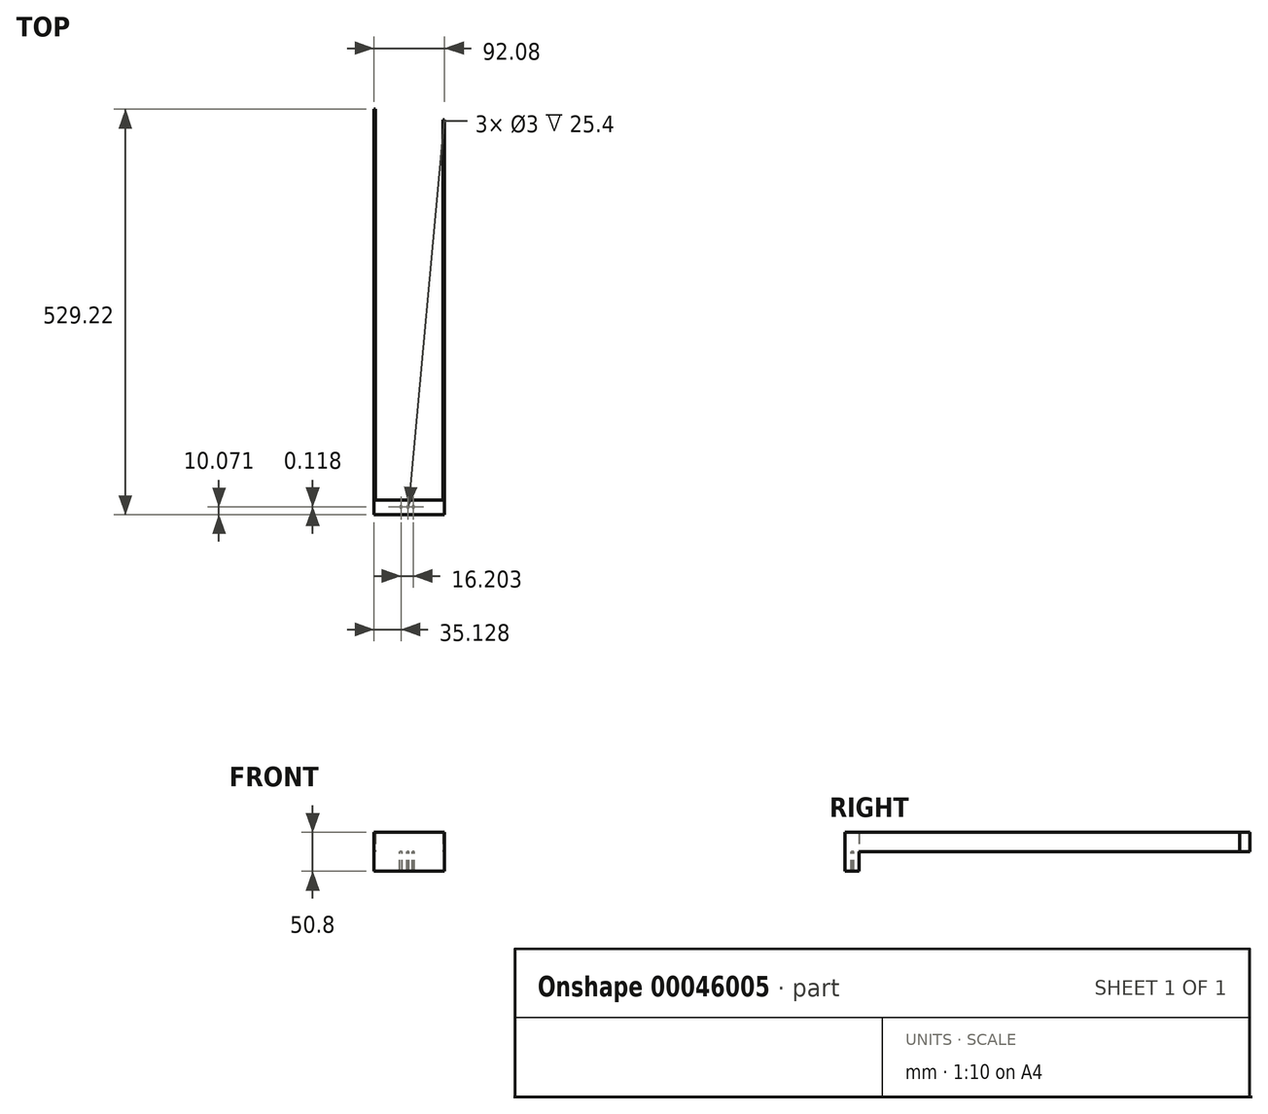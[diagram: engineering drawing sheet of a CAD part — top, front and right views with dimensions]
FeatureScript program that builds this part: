
annotation { "Feature Type Name" : "Feature", "Feature Type Description" : "" }
export const myFeature = defineFeature(function(context is Context, id is Id, definition is map)
    precondition{}
    {
        {
            var Q0;
            Q0=qCreatedBy(makeId("Top.planeOp"),FACE);
            var sketch = newSketch(context, id + "F0", { "sketchPlane" : qUnion([Q0])});
            skLineSegment(sketch, "E0.bottom", {"start": v(-47.58, 18.72) * mm, "end": v(44.5, 18.72) * mm});
            skLineSegment(sketch, "E0.top", {"start": v(-47.58, 0) * mm, "end": v(44.5, 0) * mm});
            skLineSegment(sketch, "E0.left", {"start": v(-47.58, 18.72) * mm, "end": v(-47.58, 0) * mm});
            skLineSegment(sketch, "E0.right", {"start": v(44.5, 18.72) * mm, "end": v(44.5, 0) * mm});
            skLineSegment(sketch, "E1", {"start": v(44.5, 18.72) * mm, "end": v(44.5, 515.6) * mm});
            skLineSegment(sketch, "E2", {"start": v(44.5, 515.6) * mm, "end": v(42.78, 515.6) * mm});
            skLineSegment(sketch, "E3", {"start": v(42.78, 515.6) * mm, "end": v(42.78, 0) * mm});
            skLineSegment(sketch, "E4", {"start": v(-47.58, 18.72) * mm, "end": v(-47.58, 529.22) * mm});
            skLineSegment(sketch, "E5", {"start": v(-47.58, 529.22) * mm, "end": v(-45.6, 529.22) * mm});
            skLineSegment(sketch, "E6", {"start": v(-45.6, 529.22) * mm, "end": v(-45.6, 0) * mm});
            skSolve(sketch);
        }
        {
            var Q0;
            Q0=makeQuery(id+"F0.imprint","IMPRINT",FACE,{"disambiguationData":[TD([[makeQuery(id+"F0.imprint","IMPRINT",EDGE,{"derivedFrom":sQuery(id+"F0.wireOp",EDGE,"E0.bottom")}),-1.0]])]});
            extrude(context, id + "F1", {"entities" : qUnion([Q0]), "oppositeDirection" : true, "depth" : 25.4 * mm});
        }
        {
            var Q0;
            Q0=qCreatedBy(makeId("Top.planeOp"),FACE);
            var sketch = newSketch(context, id + "F2", { "sketchPlane" : qUnion([Q0])});
            skCircle(sketch, "E7", {"center": v(3.75, 10.07) * mm, "radius": 1.5 * mm});
            skCircle(sketch, "E8", {"center": v(-3.3, 10.19) * mm, "radius": 1.5 * mm});
            skCircle(sketch, "E9", {"center": v(-12.45, 10.18) * mm, "radius": 1.5 * mm});
            skSolve(sketch);
        }
        {
            var Q0;
            Q0=sQuery(id+"F2.wireOp",VERTEX,"E7.center");
            var Q1;
            Q1=sQuery(id+"F2.wireOp",VERTEX,"E8.center");
            var Q2;
            Q2=sQuery(id+"F2.wireOp",VERTEX,"E9.center");
            var Q3;
            Q3=makeQuery(id+"F1.opExtrude","SWEPT_BODY",BODY,{"disambiguationData":[OSD([sQuery(id+"F0.wireOp",EDGE,"E0.bottom"),sQuery(id+"F0.wireOp",EDGE,"E0.top"),sQuery(id+"F0.wireOp",EDGE,"E0.left"),sQuery(id+"F0.wireOp",EDGE,"E0.right")])]});
            hole(context, id + "F3", {"style" : HoleStyle.SIMPLE, "holeDiameter" : 3 * mm, "endStyle" : HoleEndStyle.THROUGH, "locations" : qUnion([Q0, Q1, Q2]), "scope" : qUnion([Q3])});
        }
        {
            var Q0;
            Q0 = qSketchRegion(id + "F0", true);
            extrude(context, id + "F4", {"entities" : qUnion([Q0]), "operationType" : NewBodyOperationType.ADD, "depth" : 25.4 * mm});
        }
    });
